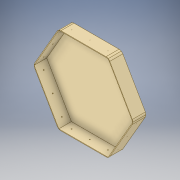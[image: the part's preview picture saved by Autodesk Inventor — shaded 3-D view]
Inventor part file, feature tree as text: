
AUTODESK INVENTOR PART (.ipt)
format: ipt  version: 2019 (Build 230136000, 136)  size: 174,080 bytes
history: native  units: mm
features: mirror x4, plane x3, extrude x2, sketch x2, fillet x2, shell x1, projected_geometry x1
ambient origin geometry x8: Origin, YZ Plane, XZ Plane, XY Plane, X Axis, Y Axis, Z Axis, Center Point
bodies: Solid1 (feature_tree)
feature tree (15):
  extrude  "Extrusion1"  Depth=30.0mm TaperAngle=0.0deg
  shell  "Shell1"  Thickness=1.5mm
  sketch  "Sketch2"  dims[d5=2.0mm d6=15.0mm d7=15.0mm d8=1.0mm d9=0.0mm d10=4.0mm d11=10.0mm d12=1.0mm]
  plane  "Work Plane1"
  plane  "Work Plane2"
  plane  "Work Plane3"
  extrude  "Extrusion2"  Depth=1.0mm
  mirror  "Mirror1"
  mirror  "Mirror2"
  mirror  "Mirror3"
  mirror  "Mirror4"
  fillet  "Fillet1"  Radius=15.0mm
  fillet  "Fillet2"  Radius=1.0mm
  sketch  "Sketch1"  dims[d0=200.0mm d2=30.0mm d3=0.0mm d4=1.5mm]
  projected_geometry  "Projected Loop1"
